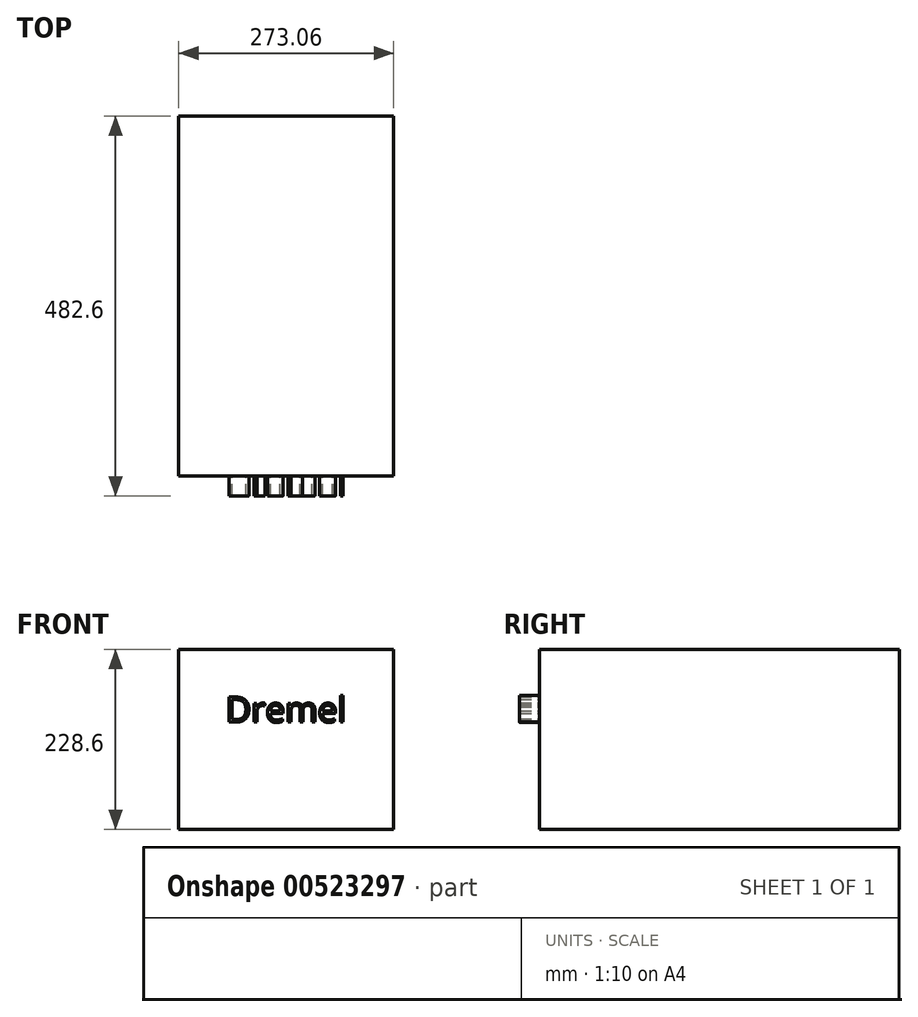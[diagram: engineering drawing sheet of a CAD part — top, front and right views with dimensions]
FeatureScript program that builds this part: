
annotation { "Feature Type Name" : "Feature", "Feature Type Description" : "" }
export const myFeature = defineFeature(function(context is Context, id is Id, definition is map)
    precondition{}
    {
        {
            var Q0;
            Q0=qCreatedBy(makeId("Front.planeOp"),FACE);
            var sketch = newSketch(context, id + "F0", { "sketchPlane" : qUnion([Q0])});
            skLineSegment(sketch, "E0.bottom", {"start": v(136.53, 114.3) * mm, "end": v(-136.53, 114.3) * mm});
            skLineSegment(sketch, "E0.top", {"start": v(136.53, -114.3) * mm, "end": v(-136.53, -114.3) * mm});
            skLineSegment(sketch, "E0.left", {"start": v(136.53, 114.3) * mm, "end": v(136.53, -114.3) * mm});
            skLineSegment(sketch, "E0.right", {"start": v(-136.53, 114.3) * mm, "end": v(-136.52, -114.3) * mm});
            skPoint(sketch, "E0.middle", {"position": v(0, 0) * mm});
            skSolve(sketch);
        }
        {
            var Q0;
            Q0=makeQuery(id+"F0.imprint","IMPRINT",FACE,{"disambiguationData":[TD([[makeQuery(id+"F0.imprint","IMPRINT",EDGE,{"derivedFrom":sQuery(id+"F0.wireOp",EDGE,"E0.bottom")}),1.0]])]});
            extrude(context, id + "F1", {"entities" : qUnion([Q0]), "depth" : 457.2 * mm, "offsetDistance" : 25.4 * mm});
        }
        {
            var Q0;
            Q0=makeQuery(id+"F1.opExtrude","CAP_FACE",FACE,{"disambiguationData":[OSD([sQuery(id+"F0.wireOp",EDGE,"E0.bottom"),sQuery(id+"F0.wireOp",EDGE,"E0.top"),sQuery(id+"F0.wireOp",EDGE,"E0.left"),sQuery(id+"F0.wireOp",EDGE,"E0.right")])],"isStart":false});
            var sketch = newSketch(context, id + "F2", { "sketchPlane" : qUnion([Q0])});
            skText(sketch, "E1", { "text": "Dremel", "fontName": "OpenSans-Regular.ttf"});
            const initialGuessF2  = {"E1": [-0.07703, 0.02199, 1, 0, 0.03207]};
            skSetInitialGuess(sketch, initialGuessF2);
            skSolve(sketch);
        }
        {
            var Q0;
            Q0 = qSketchRegion(id + "F2", true);
            extrude(context, id + "F3", {"entities" : qUnion([Q0]), "operationType" : NewBodyOperationType.ADD, "depth" : 25.4 * mm, "offsetDistance" : 25.4 * mm});
        }
    });
